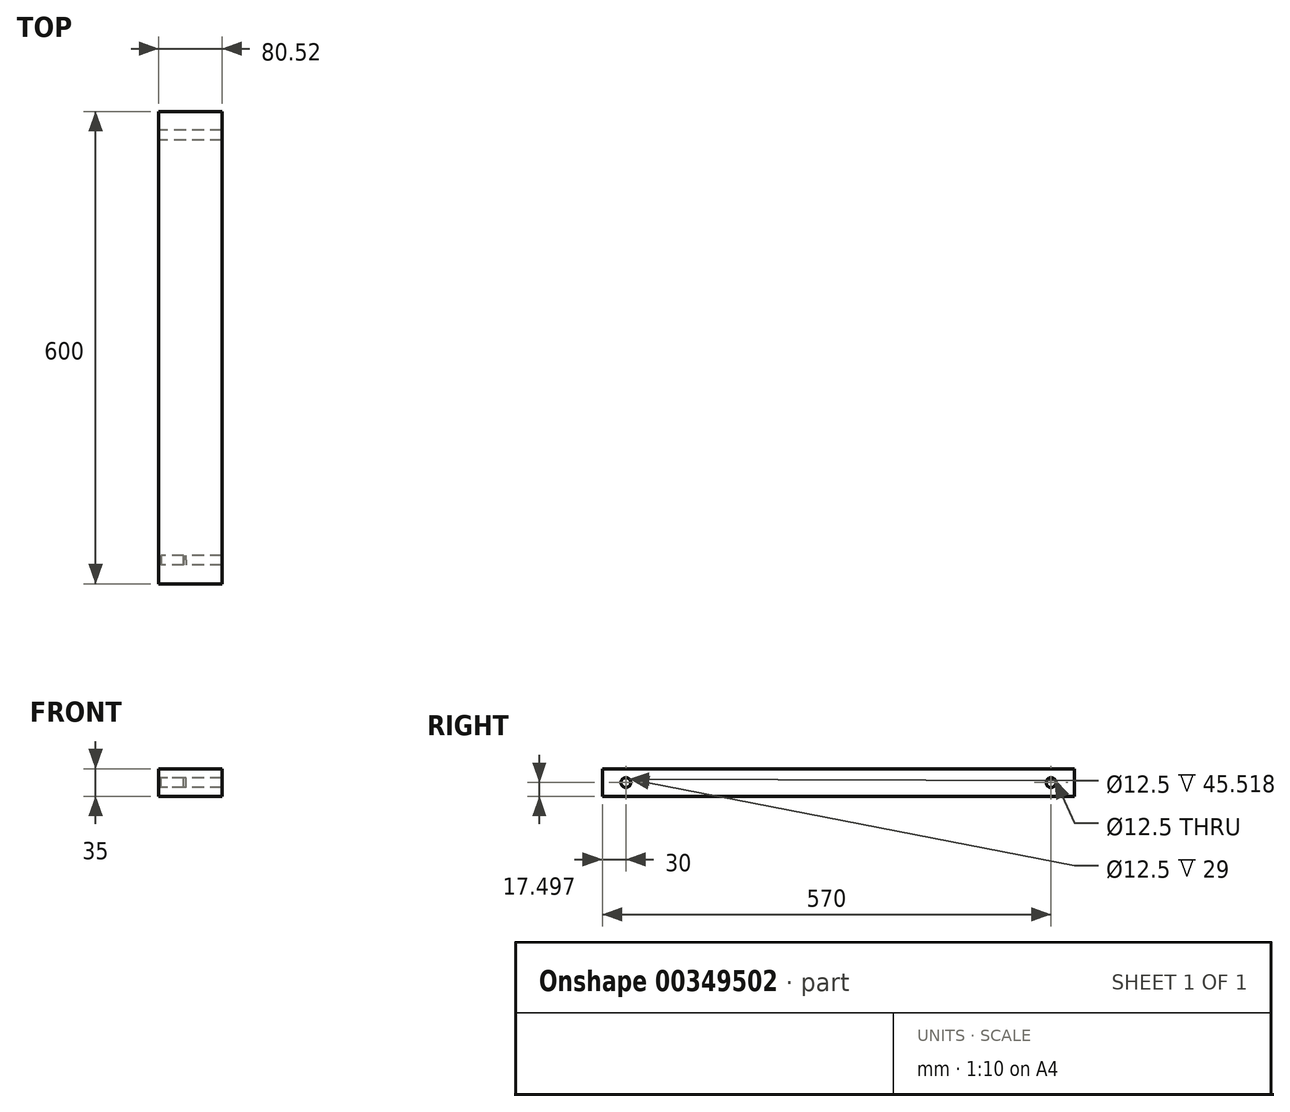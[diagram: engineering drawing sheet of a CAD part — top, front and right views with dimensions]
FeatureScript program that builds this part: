
annotation { "Feature Type Name" : "Feature", "Feature Type Description" : "" }
export const myFeature = defineFeature(function(context is Context, id is Id, definition is map)
    precondition{}
    {
        {
            var Q0;
            Q0=qCreatedBy(makeId("Front.planeOp"),FACE);
            var sketch = newSketch(context, id + "F0", { "sketchPlane" : qUnion([Q0])});
            skLineSegment(sketch, "E0.bottom", {"start": v(-71.11, -7.35) * mm, "end": v(-36.11, -7.35) * mm});
            skLineSegment(sketch, "E0.top", {"start": v(-71.11, -42.35) * mm, "end": v(-36.11, -42.35) * mm});
            skLineSegment(sketch, "E0.left", {"start": v(-71.11, -7.35) * mm, "end": v(-71.11, -42.35) * mm});
            skLineSegment(sketch, "E0.right", {"start": v(-36.11, -7.35) * mm, "end": v(-36.11, -42.35) * mm});
            skLineSegment(sketch, "E1.0", {"start": v(-39.11, -10.35) * mm, "end": v(-39.11, -39.35) * mm});
            skLineSegment(sketch, "E1.1", {"start": v(-68.11, -10.35) * mm, "end": v(-39.11, -10.35) * mm});
            skLineSegment(sketch, "E1.2", {"start": v(-68.11, -10.35) * mm, "end": v(-68.11, -39.35) * mm});
            skLineSegment(sketch, "E1.3", {"start": v(-68.11, -39.35) * mm, "end": v(-39.11, -39.35) * mm});
            skSolve(sketch);
        }
        {
            var Q0;
            Q0 = qSketchRegion(id + "F0", true);
            extrude(context, id + "F1", {"entities" : qUnion([Q0]), "depth" : 600 * mm, "symmetric" : true});
        }
        {
            var Q0;
            Q0=makeQuery(id+"F1.opExtrude","SWEPT_FACE",FACE,{"disambiguationData":[OSD([sQuery(id+"F0.wireOp",EDGE,"E0.left")])]});
            var sketch = newSketch(context, id + "F2", { "sketchPlane" : qUnion([Q0])});
            skCircle(sketch, "E2", {"center": v(-270, -24.85) * mm, "radius": 6.25 * mm});
            skCircle(sketch, "E3.MirrorC", {"center": v(270, -24.85) * mm, "radius": 6.25 * mm});
            skSolve(sketch);
        }
        {
            var Q0;
            Q0=makeQuery(id+"F2.imprint","IMPRINT",FACE,{"disambiguationData":[TD([[makeQuery(id+"F2.imprint","IMPRINT",EDGE,{"derivedFrom":sQuery(id+"F2.wireOp",EDGE,"E2")}),1.0]])]});
            extrude(context, id + "F3", {"entities" : qUnion([Q0]), "operationType" : NewBodyOperationType.REMOVE, "oppositeDirection" : true, "depth" : 35.56 * mm});
        }
        {
            var Q0;
            Q0=makeQuery(id+"F2.imprint","IMPRINT",FACE,{"disambiguationData":[TD([[makeQuery(id+"F2.imprint","IMPRINT",EDGE,{"derivedFrom":sQuery(id+"F2.wireOp",EDGE,"E3.MirrorC")}),-1.0]])]});
            extrude(context, id + "F4", {"entities" : qUnion([Q0]), "operationType" : NewBodyOperationType.ADD, "oppositeDirection" : true, "depth" : 80.52 * mm});
        }
    });
